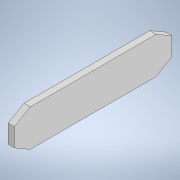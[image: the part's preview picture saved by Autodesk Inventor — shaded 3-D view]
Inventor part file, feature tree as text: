
AUTODESK INVENTOR PART (.ipt)
format: ipt  version: 2020 (Build 240168000, 168)  size: 108,544 bytes
history: native  units: in
note: dims shown in document units (in); Inventor stores cm internally (conversion verified against a paired STEP export)
features: extrude x1, sketch x1
ambient origin geometry x8: Origin, YZ Plane, XZ Plane, XY Plane, X Axis, Y Axis, Z Axis, Center Point
bodies: Solid1 (feature_tree)
feature tree (2):
  extrude  "Extrusion1"  Depth=5.9055in
  sketch  "Sketch1"  dims[d0=1.378in d1=5.9055in d2=0.2362in d3=0.0in]
